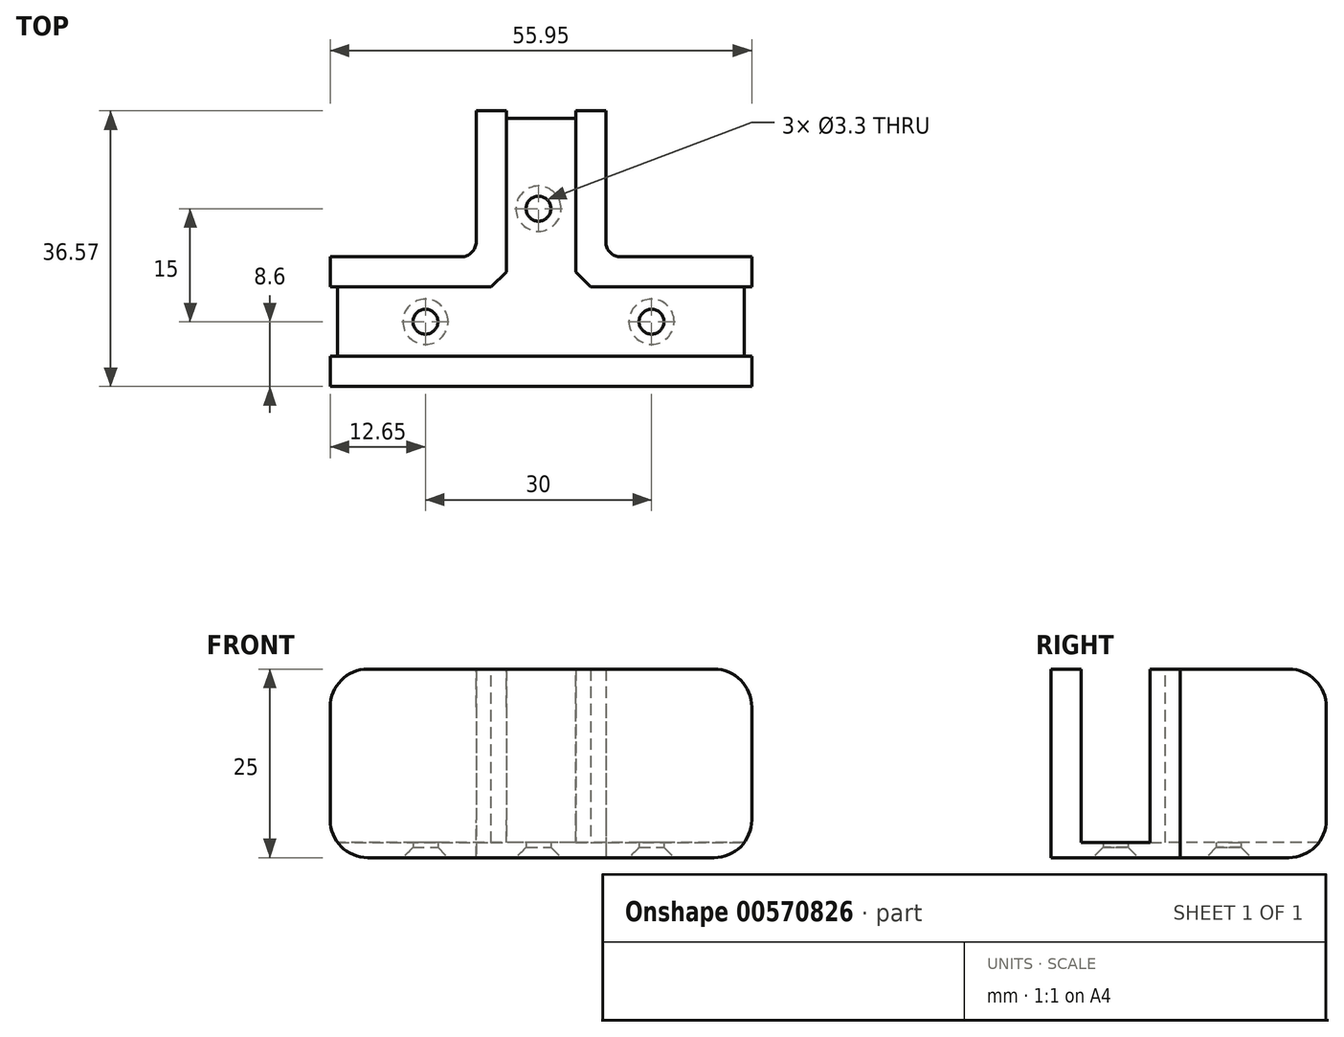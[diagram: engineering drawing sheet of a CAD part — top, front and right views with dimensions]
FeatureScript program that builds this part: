
annotation { "Feature Type Name" : "Feature", "Feature Type Description" : "" }
export const myFeature = defineFeature(function(context is Context, id is Id, definition is map)
    precondition{}
    {
        {
            var Q0;
            Q0=qCreatedBy(makeId("Top.planeOp"),FACE);
            var sketch = newSketch(context, id + "F0", { "sketchPlane" : qUnion([Q0])});
            skLineSegment(sketch, "E0", {"start": v(0, 0) * mm, "end": v(28.3, 0) * mm});
            skLineSegment(sketch, "E1", {"start": v(28.3, 9.2) * mm, "end": v(4.92, 9.2) * mm});
            skLineSegment(sketch, "E2", {"start": v(4.92, 9.2) * mm, "end": v(4.92, 32.57) * mm});
            skLineSegment(sketch, "E3", {"start": v(-4.28, 32.57) * mm, "end": v(-4.28, 9.2) * mm});
            skLineSegment(sketch, "E4", {"start": v(-4.28, 9.2) * mm, "end": v(-27.65, 9.2) * mm});
            skLineSegment(sketch, "E5", {"start": v(-27.65, 0) * mm, "end": v(0, 0) * mm});
            skLineSegment(sketch, "E6.0", {"start": v(8.92, 32.57) * mm, "end": v(-8.28, 32.57) * mm});
            skLineSegment(sketch, "E6.1", {"start": v(8.92, 13.2) * mm, "end": v(8.92, 32.57) * mm});
            skLineSegment(sketch, "E6.2", {"start": v(-8.28, 32.57) * mm, "end": v(-8.28, 13.2) * mm});
            skLineSegment(sketch, "E6.3", {"start": v(28.3, 13.2) * mm, "end": v(8.92, 13.2) * mm});
            skLineSegment(sketch, "E6.4", {"start": v(28.3, -4) * mm, "end": v(28.3, 13.2) * mm});
            skLineSegment(sketch, "E6.5", {"start": v(-8.28, 13.2) * mm, "end": v(-27.65, 13.2) * mm});
            skLineSegment(sketch, "E6.6", {"start": v(-27.65, 13.2) * mm, "end": v(-27.65, -4) * mm});
            skLineSegment(sketch, "E6.7", {"start": v(-27.65, -4) * mm, "end": v(0, -4) * mm});
            skLineSegment(sketch, "E6.8", {"start": v(0, -4) * mm, "end": v(28.3, -4) * mm});
            skSolve(sketch);
        }
        {
            var Q0;
            Q0 = qSketchRegion(id + "F0", true);
            extrude(context, id + "F1", {"entities" : qUnion([Q0]), "depth" : 2 * mm, "offsetDistance" : 25 * mm});
        }
        {
            var Q0;
            {var subQ4=sQuery(id+"F0.wireOp",EDGE,"E3");Q0=makeQuery(id+"F0.imprint","IMPRINT",FACE,{"disambiguationData":[TD([[makeQuery(id+"F0.imprint","IMPRINT",EDGE,{"derivedFrom":subQ4}),-1.0]])]});}
            var Q1;
            {var subQ3=sQuery(id+"F0.wireOp",EDGE,"E1");Q1=makeQuery(id+"F0.imprint","IMPRINT",FACE,{"disambiguationData":[TD([[makeQuery(id+"F0.imprint","IMPRINT",EDGE,{"derivedFrom":subQ3}),-1.0]])]});}
            var Q2;
            {var subQ4=sQuery(id+"F0.wireOp",EDGE,"E0");Q2=makeQuery(id+"F0.imprint","IMPRINT",FACE,{"disambiguationData":[TD([[makeQuery(id+"F0.imprint","IMPRINT",EDGE,{"derivedFrom":subQ4}),-1.0]])]});}
            extrude(context, id + "F2", {"entities" : qUnion([Q0, Q1, Q2]), "operationType" : NewBodyOperationType.ADD, "depth" : 25 * mm, "offsetDistance" : 25 * mm});
        }
        {
            var Q0;
            {var subQ0=sQuery(id+"F0.wireOp",EDGE,"E6.3");var subQ1=sQuery(id+"F0.wireOp",EDGE,"E6.1");Q0=makeQuery(id+"F2.boolean.opBoolean","MERGE",EDGE,{"derivedFrom":[makeQuery(id+"F1.opExtrude","SWEPT_EDGE",EDGE,{"disambiguationData":[OSD([subQ1,subQ0])]}),makeQuery(id+"F2.opExtrude","SWEPT_EDGE",EDGE,{"disambiguationData":[OSD([subQ1,subQ0])]})]});}
            fillet(context, id + "F3", {"entities" : qUnion([Q0]), "radius" : 2 * mm, "tangentPropagation" : true, "allowEdgeOverflow" : false});
        }
        {
            var Q0;
            {var subQ0=sQuery(id+"F0.wireOp",EDGE,"E6.4");Q0=makeQuery(id+"F2.opExtrude","CAP_EDGE",EDGE,{"disambiguationData":[OSD([subQ0]),TDD([makeQuery(id+"F0.imprint","IMPRINT",EDGE,{"disambiguationData":[TD([[makeQuery(id+"F0.imprint","INTERSECT",VERTEX,{"derivedFrom":[sQuery(id+"F0.wireOp",EDGE,"E0"),subQ0]}),1.0]])],"derivedFrom":subQ0})])],"isStart":false});}
            var Q1;
            {var subQ0=sQuery(id+"F0.wireOp",EDGE,"E6.4");Q1=makeQuery(id+"F2.opExtrude","CAP_EDGE",EDGE,{"disambiguationData":[OSD([subQ0]),TDD([makeQuery(id+"F0.imprint","IMPRINT",EDGE,{"disambiguationData":[TD([[makeQuery(id+"F0.imprint","INTERSECT",VERTEX,{"derivedFrom":[sQuery(id+"F0.wireOp",EDGE,"E1"),subQ0]}),-1.0]])],"derivedFrom":subQ0})])],"isStart":false});}
            var Q2;
            {var subQ0=sQuery(id+"F0.wireOp",EDGE,"E6.6");Q2=makeQuery(id+"F2.opExtrude","CAP_EDGE",EDGE,{"disambiguationData":[OSD([subQ0]),TDD([makeQuery(id+"F0.imprint","IMPRINT",EDGE,{"disambiguationData":[TD([[makeQuery(id+"F0.imprint","INTERSECT",VERTEX,{"derivedFrom":[sQuery(id+"F0.wireOp",EDGE,"E5"),subQ0]}),-1.0]])],"derivedFrom":subQ0})])],"isStart":false});}
            var Q3;
            {var subQ0=sQuery(id+"F0.wireOp",EDGE,"E6.6");Q3=makeQuery(id+"F2.opExtrude","CAP_EDGE",EDGE,{"disambiguationData":[OSD([subQ0]),TDD([makeQuery(id+"F0.imprint","IMPRINT",EDGE,{"disambiguationData":[TD([[makeQuery(id+"F0.imprint","INTERSECT",VERTEX,{"derivedFrom":[sQuery(id+"F0.wireOp",EDGE,"E4"),subQ0]}),1.0]])],"derivedFrom":subQ0})])],"isStart":false});}
            var Q4;
            {var subQ0=sQuery(id+"F0.wireOp",EDGE,"E6.0");Q4=makeQuery(id+"F2.opExtrude","CAP_EDGE",EDGE,{"disambiguationData":[OSD([subQ0]),TDD([makeQuery(id+"F0.imprint","IMPRINT",EDGE,{"disambiguationData":[TD([[makeQuery(id+"F0.imprint","INTERSECT",VERTEX,{"derivedFrom":[sQuery(id+"F0.wireOp",EDGE,"E3"),subQ0]}),-1.0]])],"derivedFrom":subQ0})])],"isStart":false});}
            var Q5;
            {var subQ0=sQuery(id+"F0.wireOp",EDGE,"E6.0");Q5=makeQuery(id+"F2.opExtrude","CAP_EDGE",EDGE,{"disambiguationData":[OSD([subQ0]),TDD([makeQuery(id+"F0.imprint","IMPRINT",EDGE,{"disambiguationData":[TD([[makeQuery(id+"F0.imprint","INTERSECT",VERTEX,{"derivedFrom":[sQuery(id+"F0.wireOp",EDGE,"E2"),subQ0]}),1.0]])],"derivedFrom":subQ0})])],"isStart":false});}
            var Q6;
            Q6=makeQuery(id+"F1.opExtrude","CAP_EDGE",EDGE,{"disambiguationData":[OSD([sQuery(id+"F0.wireOp",EDGE,"E6.6")])],"isStart":true});
            var Q7;
            Q7=makeQuery(id+"F1.opExtrude","CAP_EDGE",EDGE,{"disambiguationData":[OSD([sQuery(id+"F0.wireOp",EDGE,"E6.4")])],"isStart":true});
            var Q8;
            Q8=makeQuery(id+"F1.opExtrude","CAP_EDGE",EDGE,{"disambiguationData":[OSD([sQuery(id+"F0.wireOp",EDGE,"E6.0")])],"isStart":true});
            fillet(context, id + "F4", {"entities" : qUnion([Q0, Q1, Q2, Q3, Q4, Q5, Q6, Q7, Q8]), "radius" : 5 * mm, "tangentPropagation" : true, "allowEdgeOverflow" : false});
        }
        {
            var Q0;
            {var subQ0=sQuery(id+"F0.wireOp",EDGE,"E6.5");var subQ1=sQuery(id+"F0.wireOp",EDGE,"E6.2");Q0=makeQuery(id+"F2.boolean.opBoolean","MERGE",EDGE,{"derivedFrom":[makeQuery(id+"F1.opExtrude","SWEPT_EDGE",EDGE,{"disambiguationData":[OSD([subQ1,subQ0])]}),makeQuery(id+"F2.opExtrude","SWEPT_EDGE",EDGE,{"disambiguationData":[OSD([subQ1,subQ0])]})]});}
            fillet(context, id + "F5", {"entities" : qUnion([Q0]), "radius" : 2 * mm, "tangentPropagation" : true, "allowEdgeOverflow" : false});
        }
        {
            var Q0;
            Q0=makeQuery(id+"F2.opExtrude","SWEPT_EDGE",EDGE,{"disambiguationData":[OSD([sQuery(id+"F0.wireOp",EDGE,"E1"),sQuery(id+"F0.wireOp",EDGE,"E2")])]});
            var Q1;
            Q1=makeQuery(id+"F2.opExtrude","SWEPT_EDGE",EDGE,{"disambiguationData":[OSD([sQuery(id+"F0.wireOp",EDGE,"E3"),sQuery(id+"F0.wireOp",EDGE,"E4")])]});
            chamfer(context, id + "F6", {"entities" : qUnion([Q0, Q1]), "width" : 2 * mm, "tangentPropagation" : true});
        }
        {
            var Q0;
            {var subQ3=sQuery(id+"F0.wireOp",EDGE,"E0");Q0=makeQuery(id+"F0.imprint","IMPRINT",FACE,{"disambiguationData":[TD([[makeQuery(id+"F0.imprint","IMPRINT",EDGE,{"derivedFrom":subQ3}),1.0]])]});}
            var sketch = newSketch(context, id + "F7", { "sketchPlane" : qUnion([Q0])});
            skLineSegment(sketch, "E7", {"start": v(-22.65, 4.6) * mm, "end": v(23.3, 4.6) * mm});
            skPoint(sketch, "E8", {"position": v(-15, 4.6) * mm});
            skPoint(sketch, "E9", {"position": v(15, 4.6) * mm});
            skPoint(sketch, "E10", {"position": v(0, 19.6) * mm});
            skSolve(sketch);
        }
        {
            var Q0;
            Q0=sQuery(id+"F7.wireOp",VERTEX,"E8");
            var Q1;
            Q1=sQuery(id+"F7.wireOp",VERTEX,"E10");
            var Q2;
            Q2=sQuery(id+"F7.wireOp",VERTEX,"E9");
            var Q3;
            Q3=makeQuery(id+"F1.opExtrude","SWEPT_BODY",BODY,{"disambiguationData":[OSD([sQuery(id+"F0.wireOp",EDGE,"E6.0"),sQuery(id+"F0.wireOp",EDGE,"E6.1"),sQuery(id+"F0.wireOp",EDGE,"E6.2"),sQuery(id+"F0.wireOp",EDGE,"E6.3"),sQuery(id+"F0.wireOp",EDGE,"E6.4"),sQuery(id+"F0.wireOp",EDGE,"E6.5"),sQuery(id+"F0.wireOp",EDGE,"E6.6"),sQuery(id+"F0.wireOp",EDGE,"E6.7"),sQuery(id+"F0.wireOp",EDGE,"E6.8")])]});
            hole(context, id + "F8", {"style" : HoleStyle.C_SINK, "endStyle" : HoleEndStyle.THROUGH, "oppositeDirection" : true, "holeDiameter" : 3.3 * mm, "cSinkDiameter" : 6 * mm, "cSinkAngle" : 90 * degree, "majorDiameter" : 5 * mm, "isTappedThrough" : true, "tappedDepth" : 12 * mm, "tapClearance" : 3, "locations" : qUnion([Q0, Q1, Q2]), "scope" : qUnion([Q3])});
        }
    });
